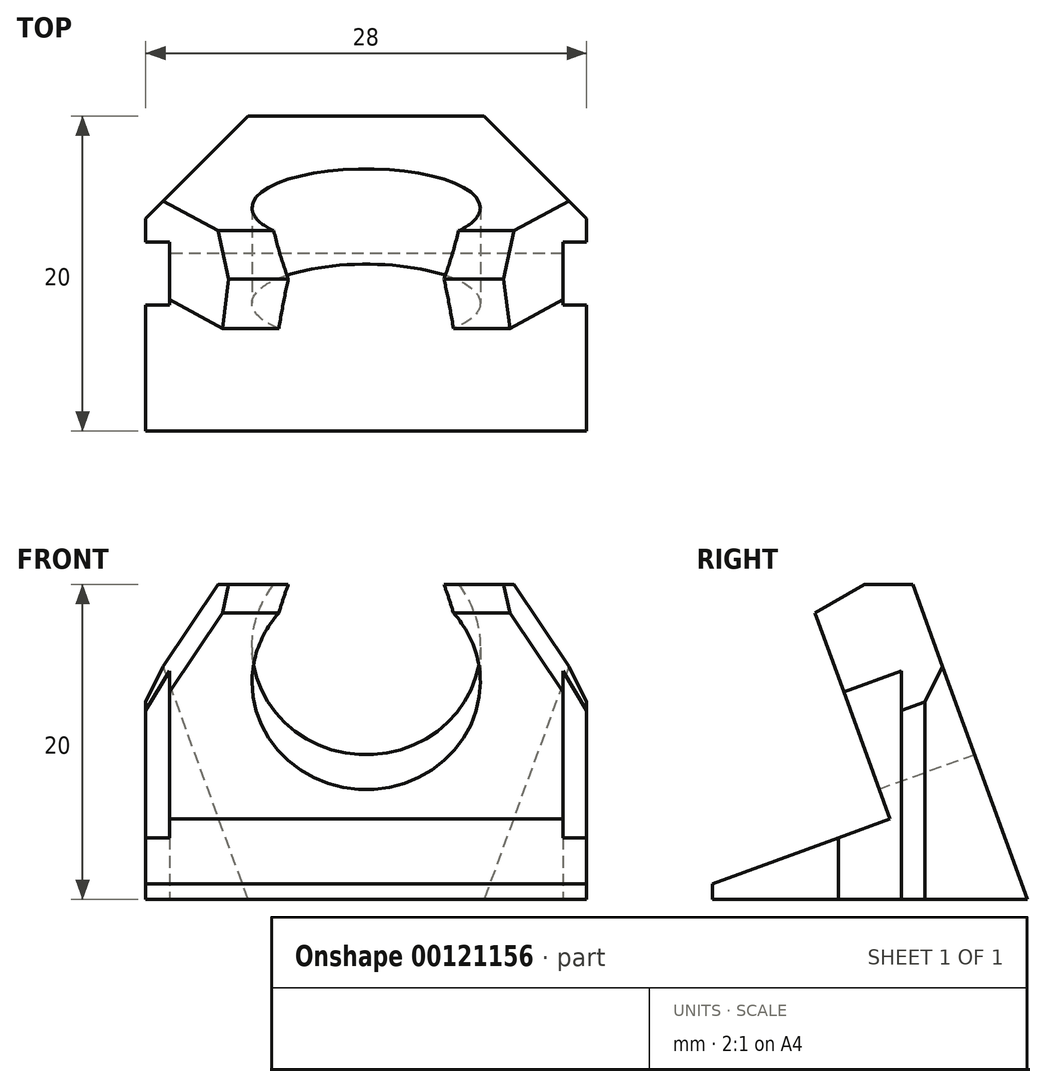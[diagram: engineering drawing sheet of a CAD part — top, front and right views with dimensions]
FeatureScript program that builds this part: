
annotation { "Feature Type Name" : "Feature", "Feature Type Description" : "" }
export const myFeature = defineFeature(function(context is Context, id is Id, definition is map)
    precondition{}
    {
        {
            var Q0;
            Q0=qCreatedBy(makeId("Top.planeOp"),FACE);
            var sketch = newSketch(context, id + "F0", { "sketchPlane" : qUnion([Q0])});
            skLineSegment(sketch, "E0.bottom", {"start": v(-14, 10) * mm, "end": v(14, 10) * mm});
            skLineSegment(sketch, "E0.top", {"start": v(-14, -10) * mm, "end": v(14, -10) * mm});
            skLineSegment(sketch, "E0.left", {"start": v(-14, 10) * mm, "end": v(-14, -10) * mm});
            skLineSegment(sketch, "E0.right", {"start": v(14, 10) * mm, "end": v(14, -10) * mm});
            skSolve(sketch);
        }
        {
            var Q0;
            Q0=makeQuery(id+"F0.imprint","IMPRINT",FACE,{"disambiguationData":[TD([[makeQuery(id+"F0.imprint","IMPRINT",EDGE,{"derivedFrom":sQuery(id+"F0.wireOp",EDGE,"E0.bottom")}),-1.0]])]});
            extrude(context, id + "F1", {"entities" : qUnion([Q0]), "depth" : 20 * mm});
        }
        {
            var Q0;
            Q0=qCreatedBy(makeId("Top.planeOp"),FACE);
            var sketch = newSketch(context, id + "F2", { "sketchPlane" : qUnion([Q0])});
            skLineSegment(sketch, "E1", {"start": v(-7.5, 10) * mm, "end": v(-14, 3.5) * mm});
            skLineSegment(sketch, "E2", {"start": v(-14, 3.5) * mm, "end": v(-14, 10) * mm});
            skLineSegment(sketch, "E3", {"start": v(-14, 10) * mm, "end": v(-7.5, 10) * mm});
            skSolve(sketch);
        }
        {
            var Q0;
            Q0=qSketchRegion(id+"F2",true);
            extrude(context, id + "F3", {"entities" : qUnion([Q0]), "depth" : 20 * mm});
        }
        {
            var Q0;
            Q0=makeQuery(id+"F3.opExtrude","SWEPT_BODY",BODY,{"disambiguationData":[OSD([sQuery(id+"F2.wireOp",EDGE,"E1"),sQuery(id+"F2.wireOp",EDGE,"E2"),sQuery(id+"F2.wireOp",EDGE,"E3")])]});
            var Q1;
            Q1=qCreatedBy(makeId("Right.planeOp"),FACE);
            mirror(context, id + "F4", {"entities" : qUnion([Q0]), "mirrorPlane" : qUnion([Q1])});
        }
        {
            var Q0;
            Q0=qCreatedBy(makeId("Right.planeOp"),FACE);
            var sketch = newSketch(context, id + "F5", { "sketchPlane" : qUnion([Q0])});
            skLineSegment(sketch, "E4", {"start": v(10, 0) * mm, "end": v(10, 27.7) * mm});
            skLineSegment(sketch, "E5", {"start": v(10, 27.7) * mm, "end": v(-0.08, 27.7) * mm});
            skLineSegment(sketch, "E6", {"start": v(-0.08, 27.7) * mm, "end": v(10, 0) * mm});
            skSolve(sketch);
        }
        {
            var Q0;
            Q0=qSketchRegion(id+"F5",true);
            extrude(context, id + "F6", {"entities" : qUnion([Q0]), "endBound" : BoundingType.SYMMETRIC, "depth" : 35 * mm});
        }
        {
            var Q0;
            Q0=qCreatedBy(makeId("Top.planeOp"),FACE);
            var sketch = newSketch(context, id + "F7", { "sketchPlane" : qUnion([Q0])});
            skLineSegment(sketch, "E7.bottom", {"start": v(-14, -2) * mm, "end": v(-12.5, -2) * mm});
            skLineSegment(sketch, "E7.top", {"start": v(-14, 2) * mm, "end": v(-12.5, 2) * mm});
            skLineSegment(sketch, "E7.left", {"start": v(-14, -2) * mm, "end": v(-14, 2) * mm});
            skLineSegment(sketch, "E7.right", {"start": v(-12.5, -2) * mm, "end": v(-12.5, 2) * mm});
            skSolve(sketch);
        }
        {
            var Q0;
            Q0=qSketchRegion(id+"F7",true);
            extrude(context, id + "F8", {"entities" : qUnion([Q0]), "depth" : 40 * mm});
        }
        {
            var Q0;
            Q0=makeQuery(id+"F8.opExtrude","SWEPT_BODY",BODY,{"disambiguationData":[OSD([sQuery(id+"F7.wireOp",EDGE,"E7.bottom"),sQuery(id+"F7.wireOp",EDGE,"E7.top"),sQuery(id+"F7.wireOp",EDGE,"E7.left"),sQuery(id+"F7.wireOp",EDGE,"E7.right")])]});
            var Q1;
            Q1=qCreatedBy(makeId("Right.planeOp"),FACE);
            mirror(context, id + "F9", {"entities" : qUnion([Q0]), "mirrorPlane" : qUnion([Q1])});
        }
        {
            var Q0;
            Q0=makeQuery(id+"F3.opExtrude","SWEPT_BODY",BODY,{"disambiguationData":[OSD([sQuery(id+"F2.wireOp",EDGE,"E1"),sQuery(id+"F2.wireOp",EDGE,"E2"),sQuery(id+"F2.wireOp",EDGE,"E3")])]});
            var Q1;
            Q1=makeQuery(id+"F4.opPattern","COPY",BODY,{"derivedFrom":makeQuery(id+"F3.opExtrude","SWEPT_BODY",BODY,{"disambiguationData":[OSD([sQuery(id+"F2.wireOp",EDGE,"E1"),sQuery(id+"F2.wireOp",EDGE,"E2"),sQuery(id+"F2.wireOp",EDGE,"E3")])]}),"instanceName":"1"});
            var Q2;
            Q2=makeQuery(id+"F6.opExtrude","SWEPT_BODY",BODY,{"disambiguationData":[OSD([sQuery(id+"F5.wireOp",EDGE,"E4"),sQuery(id+"F5.wireOp",EDGE,"E5"),sQuery(id+"F5.wireOp",EDGE,"E6")])]});
            var Q3;
            Q3=makeQuery(id+"F8.opExtrude","SWEPT_BODY",BODY,{"disambiguationData":[OSD([sQuery(id+"F7.wireOp",EDGE,"E7.bottom"),sQuery(id+"F7.wireOp",EDGE,"E7.top"),sQuery(id+"F7.wireOp",EDGE,"E7.left"),sQuery(id+"F7.wireOp",EDGE,"E7.right")])]});
            var Q4;
            Q4=makeQuery(id+"F9.opPattern","COPY",BODY,{"derivedFrom":makeQuery(id+"F8.opExtrude","SWEPT_BODY",BODY,{"disambiguationData":[OSD([sQuery(id+"F7.wireOp",EDGE,"E7.bottom"),sQuery(id+"F7.wireOp",EDGE,"E7.top"),sQuery(id+"F7.wireOp",EDGE,"E7.left"),sQuery(id+"F7.wireOp",EDGE,"E7.right")])]}),"instanceName":"1"});
            var Q5;
            Q5=makeQuery(id+"F1.opExtrude","SWEPT_BODY",BODY,{"disambiguationData":[OSD([sQuery(id+"F0.wireOp",EDGE,"E0.bottom"),sQuery(id+"F0.wireOp",EDGE,"E0.top"),sQuery(id+"F0.wireOp",EDGE,"E0.left"),sQuery(id+"F0.wireOp",EDGE,"E0.right")])]});
            booleanBodies(context, id + "F10", {"operationType" : BooleanOperationType.SUBTRACTION, "tools" : qUnion([Q0, Q1, Q2, Q3, Q4]), "targets" : qUnion([Q5])});
        }
        {
            var Q0;
            Q0=qCreatedBy(makeId("Right.planeOp"),FACE);
            var sketch = newSketch(context, id + "F11", { "sketchPlane" : qUnion([Q0])});
            skLineSegment(sketch, "E8", {"start": v(-10, 1) * mm, "end": v(1.28, 5.1) * mm});
            skLineSegment(sketch, "E9", {"start": v(1.28, 5.1) * mm, "end": v(-10, 36.09) * mm});
            skLineSegment(sketch, "E10", {"start": v(-10, 36.09) * mm, "end": v(-10, 1) * mm});
            skSolve(sketch);
        }
        {
            var Q0;
            Q0=makeQuery(id+"F11.imprint","IMPRINT",FACE,{"disambiguationData":[TD([[makeQuery(id+"F11.imprint","IMPRINT",EDGE,{"derivedFrom":sQuery(id+"F11.wireOp",EDGE,"E8")}),1.0]])]});
            extrude(context, id + "F12", {"entities" : qUnion([Q0]), "endBound" : BoundingType.SYMMETRIC, "depth" : 30 * mm});
        }
        {
            var Q0;
            Q0=makeQuery(id+"F12.opExtrude","SWEPT_BODY",BODY,{"disambiguationData":[OSD([sQuery(id+"F11.wireOp",EDGE,"E8"),sQuery(id+"F11.wireOp",EDGE,"E9"),sQuery(id+"F11.wireOp",EDGE,"E10")])]});
            var Q1;
            Q1=makeQuery(id+"F1.opExtrude","SWEPT_BODY",BODY,{"disambiguationData":[OSD([sQuery(id+"F0.wireOp",EDGE,"E0.bottom"),sQuery(id+"F0.wireOp",EDGE,"E0.top"),sQuery(id+"F0.wireOp",EDGE,"E0.left"),sQuery(id+"F0.wireOp",EDGE,"E0.right")])]});
            booleanBodies(context, id + "F13", {"operationType" : BooleanOperationType.SUBTRACTION, "tools" : qUnion([Q0]), "targets" : qUnion([Q1])});
        }
        {
            var Q0;
            Q0=makeQuery(id+"F13.opBoolean","COPY",FACE,{"derivedFrom":makeQuery(id+"F12.opExtrude","SWEPT_FACE",FACE,{"disambiguationData":[OSD([sQuery(id+"F11.wireOp",EDGE,"E9")])]})});
            var sketch = newSketch(context, id + "F14", { "sketchPlane" : qUnion([Q0])});
            skLineSegment(sketch, "E11.bottom", {"start": v(0, 4.36) * mm, "end": v(9.74, 4.36) * mm});
            skLineSegment(sketch, "E11.top", {"start": v(0, 13.6) * mm, "end": v(9.74, 13.6) * mm});
            skLineSegment(sketch, "E11.left", {"start": v(0, 4.36) * mm, "end": v(0, 13.6) * mm});
            skLineSegment(sketch, "E11.right", {"start": v(9.74, 4.36) * mm, "end": v(9.74, 13.6) * mm});
            skSolve(sketch);
        }
        {
            var Q0;
            Q0=sQuery(id+"F14.wireOp",VERTEX,"E11.left.end");
            var Q1;
            Q1=makeQuery(id+"F1.opExtrude","SWEPT_BODY",BODY,{"disambiguationData":[OSD([sQuery(id+"F0.wireOp",EDGE,"E0.bottom"),sQuery(id+"F0.wireOp",EDGE,"E0.top"),sQuery(id+"F0.wireOp",EDGE,"E0.left"),sQuery(id+"F0.wireOp",EDGE,"E0.right")])]});
            hole(context, id + "F15", {"style" : HoleStyle.SIMPLE, "endStyle" : HoleEndStyle.THROUGH, "holeDiameter" : 14.5 * mm, "locations" : qUnion([Q0]), "scope" : qUnion([Q1]), "isTappedThrough" : true});
        }
        {
            var Q0;
            Q0=qCreatedBy(makeId("Right.planeOp"),FACE);
            var sketch = newSketch(context, id + "F16", { "sketchPlane" : qUnion([Q0])});
            skLineSegment(sketch, "E12", {"start": v(0, 20.2) * mm, "end": v(-6.93, 16.2) * mm});
            skLineSegment(sketch, "E13", {"start": v(-6.93, 16.2) * mm, "end": v(-9.24, 20.2) * mm});
            skLineSegment(sketch, "E14", {"start": v(-9.24, 20.2) * mm, "end": v(0, 20.2) * mm});
            skSolve(sketch);
        }
        {
            var Q0;
            Q0=qSketchRegion(id+"F16",true);
            extrude(context, id + "F17", {"entities" : qUnion([Q0]), "endBound" : BoundingType.SYMMETRIC, "depth" : 40 * mm});
        }
        {
            var Q0;
            Q0=makeQuery(id+"F10.opBoolean","COPY",FACE,{"derivedFrom":makeQuery(id+"F6.opExtrude","SWEPT_FACE",FACE,{"disambiguationData":[OSD([sQuery(id+"F5.wireOp",EDGE,"E6")])]})});
            var sketch = newSketch(context, id + "F18", { "sketchPlane" : qUnion([Q0])});
            skLineSegment(sketch, "E15", {"start": v(4, 26.4) * mm, "end": v(14, 10.58) * mm});
            skLineSegment(sketch, "E16", {"start": v(14, 10.58) * mm, "end": v(14, 26.4) * mm});
            skLineSegment(sketch, "E17", {"start": v(14, 26.4) * mm, "end": v(4, 26.4) * mm});
            skSolve(sketch);
        }
        {
            var Q0;
            Q0=qSketchRegion(id+"F18",true);
            extrude(context, id + "F19", {"entities" : qUnion([Q0]), "endBound" : BoundingType.SYMMETRIC, "depth" : 25 * mm});
        }
        {
            var Q0;
            Q0=makeQuery(id+"F19.opExtrude","SWEPT_BODY",BODY,{"disambiguationData":[OSD([sQuery(id+"F18.wireOp",EDGE,"E15"),sQuery(id+"F18.wireOp",EDGE,"E16"),sQuery(id+"F18.wireOp",EDGE,"E17")])]});
            var Q1;
            Q1=qCreatedBy(makeId("Right.planeOp"),FACE);
            mirror(context, id + "F20", {"entities" : qUnion([Q0]), "mirrorPlane" : qUnion([Q1])});
        }
        {
            var Q0;
            Q0=makeQuery(id+"F20.opPattern","COPY",BODY,{"derivedFrom":makeQuery(id+"F19.opExtrude","SWEPT_BODY",BODY,{"disambiguationData":[OSD([sQuery(id+"F18.wireOp",EDGE,"E15"),sQuery(id+"F18.wireOp",EDGE,"E16"),sQuery(id+"F18.wireOp",EDGE,"E17")])]}),"instanceName":"1"});
            var Q1;
            Q1=makeQuery(id+"F19.opExtrude","SWEPT_BODY",BODY,{"disambiguationData":[OSD([sQuery(id+"F18.wireOp",EDGE,"E15"),sQuery(id+"F18.wireOp",EDGE,"E16"),sQuery(id+"F18.wireOp",EDGE,"E17")])]});
            var Q2;
            Q2=makeQuery(id+"F17.opExtrude","SWEPT_BODY",BODY,{"disambiguationData":[OSD([sQuery(id+"F16.wireOp",EDGE,"E12"),sQuery(id+"F16.wireOp",EDGE,"E13"),sQuery(id+"F16.wireOp",EDGE,"E14")])]});
            var Q3;
            Q3=makeQuery(id+"F1.opExtrude","SWEPT_BODY",BODY,{"disambiguationData":[OSD([sQuery(id+"F0.wireOp",EDGE,"E0.bottom"),sQuery(id+"F0.wireOp",EDGE,"E0.top"),sQuery(id+"F0.wireOp",EDGE,"E0.left"),sQuery(id+"F0.wireOp",EDGE,"E0.right")])]});
            booleanBodies(context, id + "F21", {"operationType" : BooleanOperationType.SUBTRACTION, "tools" : qUnion([Q0, Q1, Q2]), "targets" : qUnion([Q3])});
        }
    });
